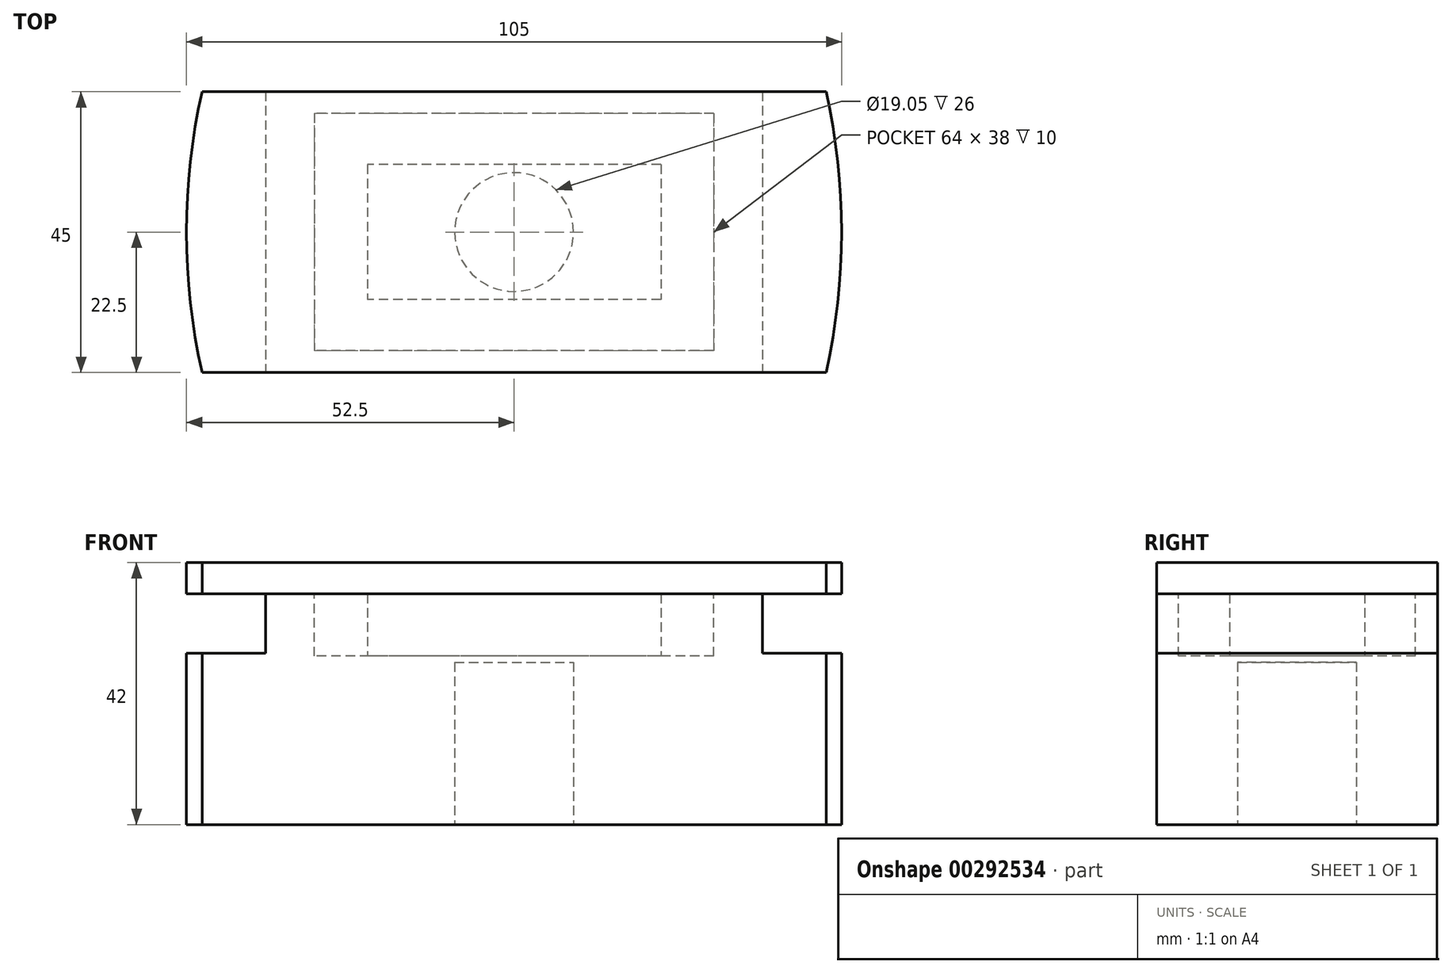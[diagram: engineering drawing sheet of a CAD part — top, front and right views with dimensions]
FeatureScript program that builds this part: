
annotation { "Feature Type Name" : "Feature", "Feature Type Description" : "" }
export const myFeature = defineFeature(function(context is Context, id is Id, definition is map)
    precondition{}
    {
        {
            var Q0;
            Q0=qCreatedBy(makeId("Top.planeOp"),FACE);
            var sketch = newSketch(context, id + "F0", { "sketchPlane" : qUnion([Q0])});
            skPoint(sketch, "E0.middle", {"position": v(0, 0) * mm});
            skPoint(sketch, "E1", {"position": v(-50, -22.5) * mm});
            skPoint(sketch, "E2.MirrorP", {"position": v(50, -22.5) * mm});
            skPoint(sketch, "E3.MirrorP", {"position": v(50, 22.5) * mm});
            skPoint(sketch, "E4.MirrorP", {"position": v(-50, 22.5) * mm});
            skPoint(sketch, "E5", {"position": v(-52.5, 0) * mm});
            skPoint(sketch, "E6", {"position": v(52.5, 0) * mm});
            skArc(sketch, "E7", {"start": v(-50, 22.5) * mm, "mid": v(-52.5, 0) * mm, "end": v(-50, -22.5) * mm});
            skArc(sketch, "E8", {"start": v(50, -22.5) * mm, "mid": v(52.5, 0) * mm, "end": v(50, 22.5) * mm});
            skLineSegment(sketch, "E9", {"start": v(-50, 22.5) * mm, "end": v(50, 22.5) * mm});
            skLineSegment(sketch, "E10", {"start": v(50, -22.5) * mm, "end": v(-50, -22.5) * mm});
            skSolve(sketch);
        }
        {
            var Q0;
            Q0 = qSketchRegion(id + "F0", true);
            extrude(context, id + "F1", {"entities" : qUnion([Q0]), "oppositeDirection" : true, "depth" : 37 * mm});
        }
        {
            var Q0;
            Q0=makeQuery(id+"F1.opExtrude","CAP_FACE",FACE,{"disambiguationData":[OSD([sQuery(id+"F0.wireOp",EDGE,"E7"),sQuery(id+"F0.wireOp",EDGE,"E8"),sQuery(id+"F0.wireOp",EDGE,"E9"),sQuery(id+"F0.wireOp",EDGE,"E10")])],"isStart":true});
            var sketch = newSketch(context, id + "F2", { "sketchPlane" : qUnion([Q0])});
            skLineSegment(sketch, "E11.bottom", {"start": v(32, 19) * mm, "end": v(-32, 19) * mm});
            skLineSegment(sketch, "E11.top", {"start": v(32, -19) * mm, "end": v(-32, -19) * mm});
            skLineSegment(sketch, "E11.left", {"start": v(32, 19) * mm, "end": v(32, -19) * mm});
            skLineSegment(sketch, "E11.right", {"start": v(-32, 19) * mm, "end": v(-32, -19) * mm});
            skPoint(sketch, "E11.middle", {"position": v(0, 0) * mm});
            skSolve(sketch);
        }
        {
            var Q0;
            Q0 = qSketchRegion(id + "F2", true);
            extrude(context, id + "F3", {"entities" : qUnion([Q0]), "operationType" : NewBodyOperationType.REMOVE, "oppositeDirection" : true, "depth" : 10 * mm});
        }
        {
            var Q0;
            Q0=makeQuery(id+"F1.opExtrude","CAP_FACE",FACE,{"disambiguationData":[OSD([sQuery(id+"F0.wireOp",EDGE,"E7"),sQuery(id+"F0.wireOp",EDGE,"E8"),sQuery(id+"F0.wireOp",EDGE,"E9"),sQuery(id+"F0.wireOp",EDGE,"E10")])],"isStart":true});
            var sketch = newSketch(context, id + "F4", { "sketchPlane" : qUnion([Q0])});
            skPoint(sketch, "E12", {"position": v(39.8, 22.5) * mm});
            skPoint(sketch, "E13.MirrorP", {"position": v(-39.8, 22.5) * mm});
            skPoint(sketch, "E14.MirrorP", {"position": v(-39.8, -22.5) * mm});
            skPoint(sketch, "E15.MirrorP", {"position": v(39.8, -22.5) * mm});
            skLineSegment(sketch, "E16", {"start": v(-39.8, 22.5) * mm, "end": v(-39.8, -22.5) * mm});
            skLineSegment(sketch, "E17", {"start": v(39.8, 22.5) * mm, "end": v(39.8, -22.5) * mm});
            skSolve(sketch);
        }
        {
            var Q0;
            Q0 = qSketchRegion(id + "F4", true);
            var Q1;
            {var subQ0=sQuery(id+"F4.wireOp",EDGE,"E16");Q1=makeQuery(id+"F4.imprint","IMPRINT",FACE,{"disambiguationData":[TD([[makeQuery(id+"F4.imprint","IMPRINT",EDGE,{"derivedFrom":subQ0}),-1.0]])]});}
            var Q2;
            {var subQ0=sQuery(id+"F4.wireOp",EDGE,"E17");Q2=makeQuery(id+"F4.imprint","IMPRINT",FACE,{"disambiguationData":[TD([[makeQuery(id+"F4.imprint","IMPRINT",EDGE,{"derivedFrom":subQ0}),1.0]])]});}
            extrude(context, id + "F5", {"entities" : qUnion([Q0, Q1, Q2]), "operationType" : NewBodyOperationType.REMOVE, "oppositeDirection" : true, "depth" : 9.53 * mm});
        }
        {
            var Q0;
            Q0=makeQuery(id+"F3.boolean.opBoolean","COPY",FACE,{"derivedFrom":makeQuery(id+"F3.opExtrude","CAP_FACE",FACE,{"disambiguationData":[OSD([sQuery(id+"F2.wireOp",EDGE,"E11.bottom"),sQuery(id+"F2.wireOp",EDGE,"E11.top"),sQuery(id+"F2.wireOp",EDGE,"E11.left"),sQuery(id+"F2.wireOp",EDGE,"E11.right")])],"isStart":false})});
            var sketch = newSketch(context, id + "F6", { "sketchPlane" : qUnion([Q0])});
            skLineSegment(sketch, "E18.bottom", {"start": v(23.52, 10.83) * mm, "end": v(-23.53, 10.82) * mm});
            skLineSegment(sketch, "E18.top", {"start": v(23.53, -10.82) * mm, "end": v(-23.52, -10.83) * mm});
            skLineSegment(sketch, "E18.left", {"start": v(23.52, 10.83) * mm, "end": v(23.53, -10.82) * mm});
            skLineSegment(sketch, "E18.right", {"start": v(-23.53, 10.82) * mm, "end": v(-23.52, -10.83) * mm});
            skPoint(sketch, "E18.middle", {"position": v(0, 0) * mm});
            skSolve(sketch);
        }
        {
            var Q0;
            Q0=makeQuery(id+"F6.imprint","IMPRINT",FACE,{"disambiguationData":[TD([[makeQuery(id+"F6.imprint","IMPRINT",EDGE,{"derivedFrom":sQuery(id+"F6.wireOp",EDGE,"E18.bottom")}),1.0]])]});
            extrude(context, id + "F7", {"entities" : qUnion([Q0]), "depth" : 10 * mm});
        }
        {
            var Q0;
            Q0=makeQuery(id+"F7.opExtrude","CAP_FACE",FACE,{"disambiguationData":[OSD([sQuery(id+"F6.wireOp",EDGE,"E18.bottom"),sQuery(id+"F6.wireOp",EDGE,"E18.top"),sQuery(id+"F6.wireOp",EDGE,"E18.left"),sQuery(id+"F6.wireOp",EDGE,"E18.right")])],"isStart":false});
            var sketch = newSketch(context, id + "F8", { "sketchPlane" : qUnion([Q0])});
            skPoint(sketch, "E19.middle", {"position": v(0, 0) * mm});
            skPoint(sketch, "E20", {"position": v(-50, -22.5) * mm});
            skPoint(sketch, "E21.MirrorP", {"position": v(50, -22.5) * mm});
            skPoint(sketch, "E22.MirrorP", {"position": v(50, 22.5) * mm});
            skPoint(sketch, "E23.MirrorP", {"position": v(-50, 22.5) * mm});
            skPoint(sketch, "E24", {"position": v(-52.5, 0) * mm});
            skPoint(sketch, "E25", {"position": v(52.5, 0) * mm});
            skArc(sketch, "E26", {"start": v(-50, 22.5) * mm, "mid": v(-52.5, 0) * mm, "end": v(-50, -22.5) * mm});
            skArc(sketch, "E27", {"start": v(50, -22.5) * mm, "mid": v(52.5, 0) * mm, "end": v(50, 22.5) * mm});
            skLineSegment(sketch, "E28", {"start": v(-50, 22.5) * mm, "end": v(50, 22.5) * mm});
            skLineSegment(sketch, "E29", {"start": v(50, -22.5) * mm, "end": v(-50, -22.5) * mm});
            skSolve(sketch);
        }
        {
            var Q0;
            Q0 = qSketchRegion(id + "F8", true);
            extrude(context, id + "F9", {"entities" : qUnion([Q0]), "depth" : 5 * mm});
        }
        {
            var Q0;
            Q0=makeQuery(id+"F1.opExtrude","CAP_FACE",FACE,{"disambiguationData":[OSD([sQuery(id+"F0.wireOp",EDGE,"E7"),sQuery(id+"F0.wireOp",EDGE,"E8"),sQuery(id+"F0.wireOp",EDGE,"E9"),sQuery(id+"F0.wireOp",EDGE,"E10")])],"isStart":false});
            var sketch = newSketch(context, id + "F10", { "sketchPlane" : qUnion([Q0])});
            skPoint(sketch, "E30", {"position": v(0, 0) * mm});
            skCircle(sketch, "E31", {"center": v(0, 0) * mm, "radius": 9.53 * mm});
            skSolve(sketch);
        }
        {
            var Q0;
            Q0=makeQuery(id+"F10.imprint","IMPRINT",FACE,{"disambiguationData":[TD([[makeQuery(id+"F10.imprint","IMPRINT",EDGE,{"derivedFrom":sQuery(id+"F10.wireOp",EDGE,"E31")}),1.0]])]});
            extrude(context, id + "F11", {"entities" : qUnion([Q0]), "operationType" : NewBodyOperationType.REMOVE, "oppositeDirection" : true, "depth" : 26 * mm});
        }
    });
